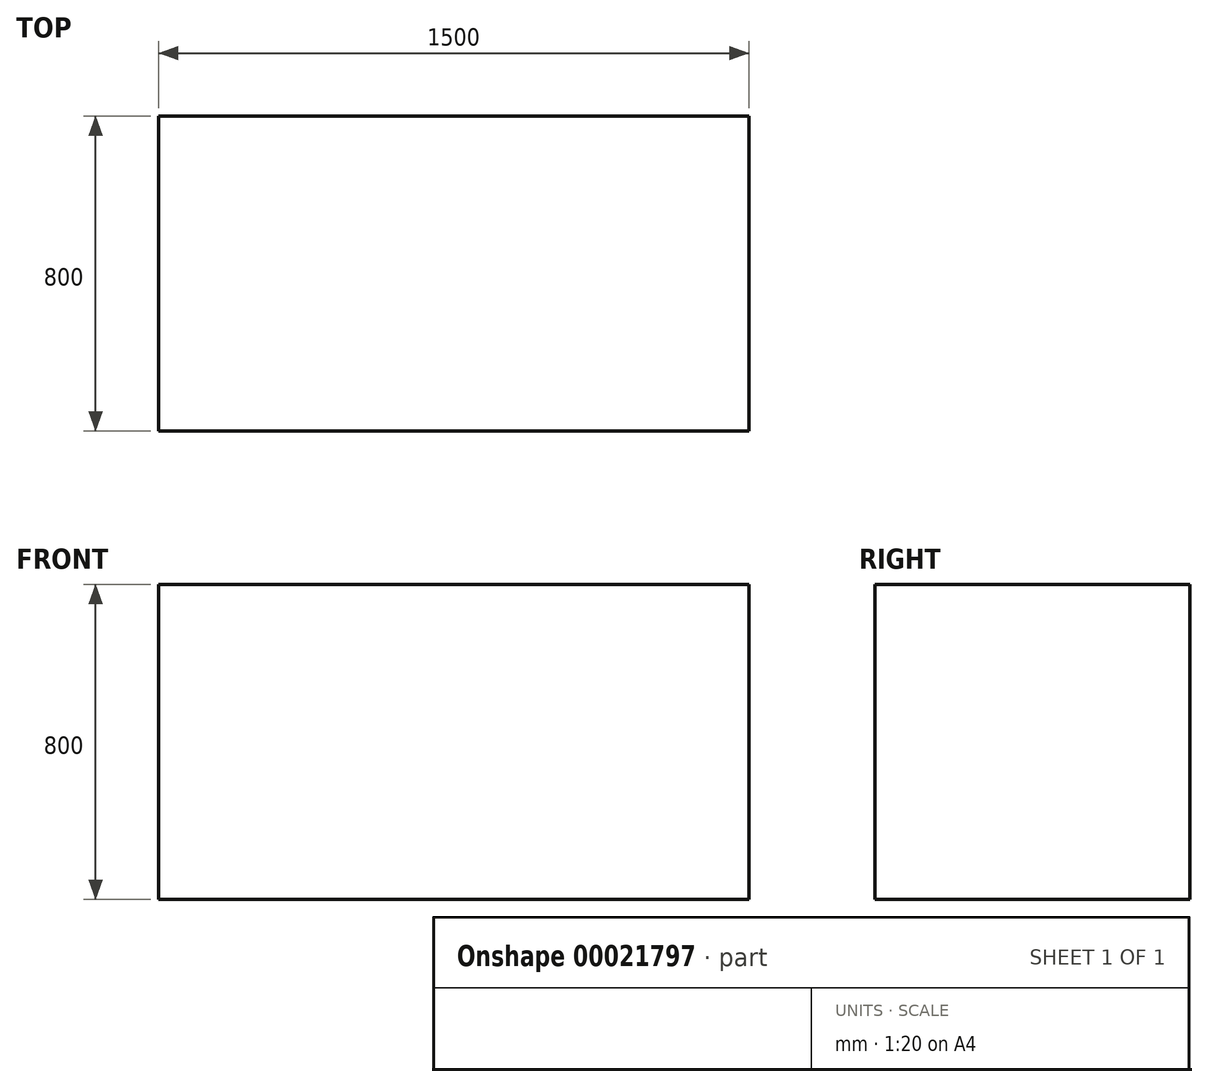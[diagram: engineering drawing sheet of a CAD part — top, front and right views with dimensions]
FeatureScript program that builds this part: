
annotation { "Feature Type Name" : "Feature", "Feature Type Description" : "" }
export const myFeature = defineFeature(function(context is Context, id is Id, definition is map)
    precondition{}
    {
        {
            var Q0;
            Q0=qCreatedBy(makeId("Top.planeOp"),FACE);
            var sketch = newSketch(context, id + "F0", { "sketchPlane" : qUnion([Q0])});
            skLineSegment(sketch, "E0.bottom", {"start": v(0, 0) * mm, "end": v(1500, 0) * mm});
            skLineSegment(sketch, "E0.top", {"start": v(0, 800) * mm, "end": v(1500, 800) * mm});
            skLineSegment(sketch, "E0.left", {"start": v(0, 0) * mm, "end": v(0, 800) * mm});
            skLineSegment(sketch, "E0.right", {"start": v(1500, 0) * mm, "end": v(1500, 800) * mm});
            skSolve(sketch);
        }
        {
            var Q0;
            Q0=makeQuery(id+"F0.imprint","IMPRINT",FACE,{"disambiguationData":[TD([[makeQuery(id+"F0.imprint","IMPRINT",EDGE,{"derivedFrom":sQuery(id+"F0.wireOp",EDGE,"E0.bottom")}),1.0]])]});
            extrude(context, id + "F1", {"entities" : qUnion([Q0]), "depth" : 800 * mm});
        }
    });
